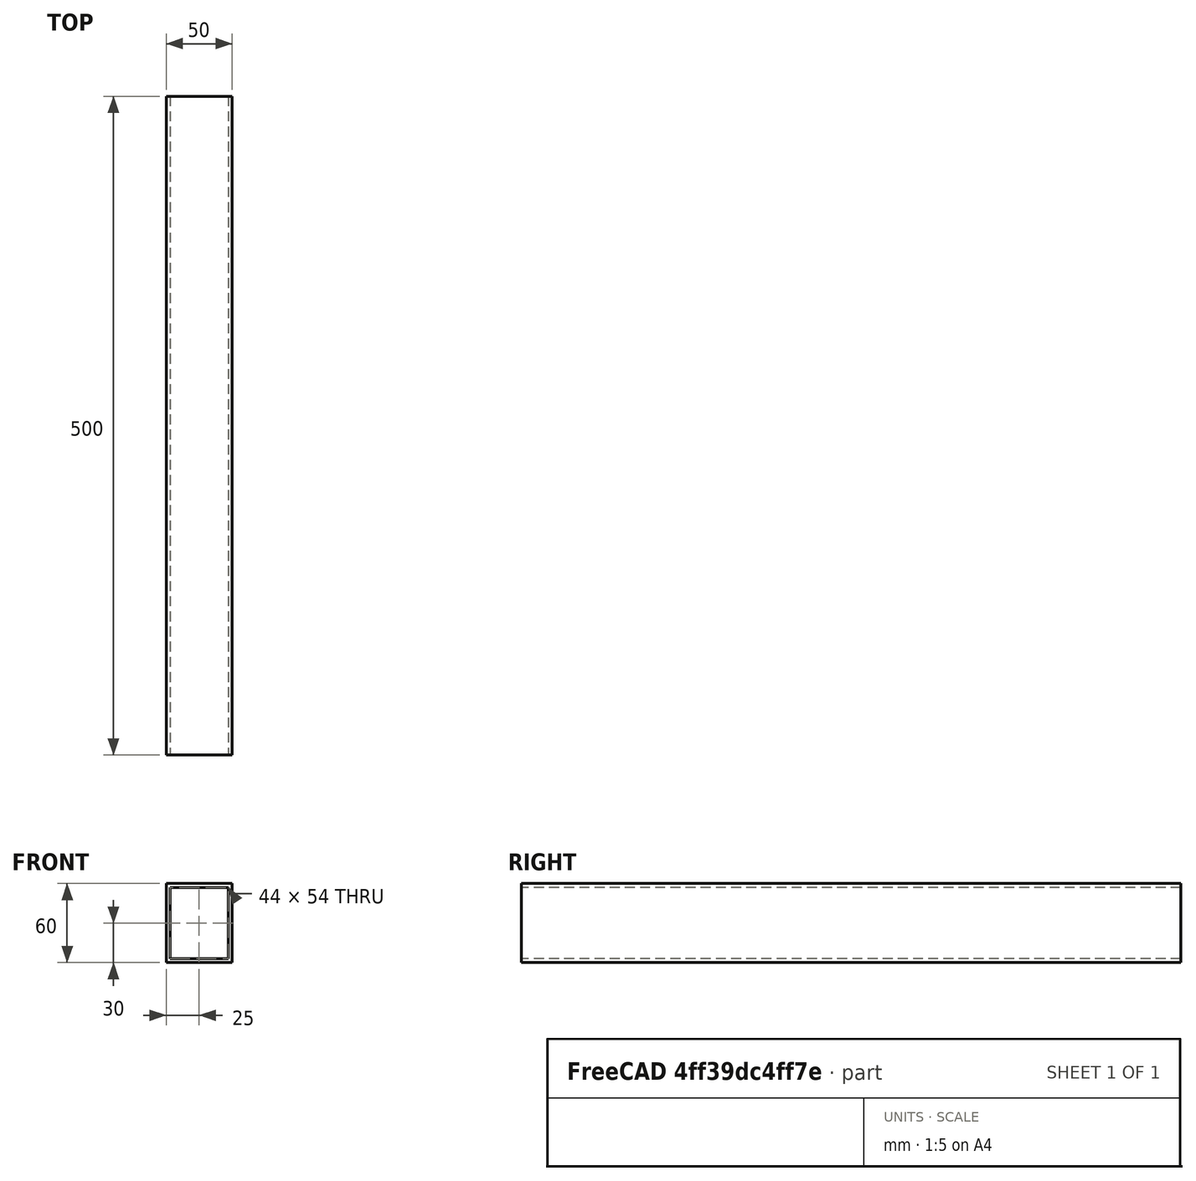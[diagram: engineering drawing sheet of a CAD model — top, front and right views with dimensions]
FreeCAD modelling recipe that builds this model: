
FCSTD DOCUMENT  (FreeCAD 0.20R29177 +426 (Git))
Label: beam_cross
License: All rights reserved
LicenseURL: http://en.wikipedia.org/wiki/All_rights_reserved
objects: Sketcher::SketchObject×1, PartDesign::Pad×1, PartDesign::Body×1
note: 4 computed .brp shape members not serialized (recipe doc carries the construction recipe); baked Part::Feature solids carry a one-line shape summary decoded from their .brp

FEATURE [Sketcher::SketchObject] Sketch
  FullyConstrained = true
  MapMode = 5
  Placement = pos=(0,0,0) rot=(1,0,0;1.5708rad)
  Support = -> [XZ_Plane]
  sketch-geometry (8):
    g0: LineSegment StartX=0 StartY=0 StartZ=0 EndX=50 EndY=0 EndZ=0
    g1: LineSegment StartX=50 StartY=0 StartZ=0 EndX=50 EndY=60 EndZ=0
    g2: LineSegment StartX=50 StartY=60 StartZ=0 EndX=0 EndY=60 EndZ=0
    g3: LineSegment StartX=0 StartY=60 StartZ=0 EndX=0 EndY=0 EndZ=0
    g4: LineSegment StartX=3 StartY=57 StartZ=0 EndX=47 EndY=57 EndZ=0
    g5: LineSegment StartX=47 StartY=57 StartZ=0 EndX=47 EndY=3 EndZ=0
    g6: LineSegment StartX=47 StartY=3 StartZ=0 EndX=3 EndY=3 EndZ=0
    g7: LineSegment StartX=3 StartY=3 StartZ=0 EndX=3 EndY=57 EndZ=0
  constraints (23):
    c: Coincident(g0,g1)
    c: Coincident(g1,g2)
    c: Coincident(g2,g3)
    c: Coincident(g3,g0)
    c: Horizontal(g0)
    c: Horizontal(g2)
    c: Vertical(g1)
    c: Vertical(g3)
    c: Coincident(g0,g-1)
    c: DistanceX(g2,g2) = 50
    c: DistanceY(g1,g1) = 60
    c: Coincident(g4,g5)
    c: Coincident(g5,g6)
    c: Coincident(g6,g7)
    c: Coincident(g7,g4)
    c: Horizontal(g4)
    c: Horizontal(g6)
    c: Vertical(g5)
    c: Vertical(g7)
    c: DistanceY(g4,g1) = 3
    c: DistanceX(g4,g1) = 3
    c: DistanceX(g0,g6) = 3
    c: DistanceY(g0,g6) = 3
FEATURE [PartDesign::Pad] Pad
  Direction = (0,-1,-2e-16)
  Length = 500
  Length2 = 10
  Placement = pos=(0,0,0) rot=(1,0,0;1.5708rad)
  Profile = -> Sketch
  ReferenceAxis = -> Sketch [N_Axis]
  Refine = true
  Type = 0
FEATURE [PartDesign::Body] Body
  Group = -> [Sketch,Pad]
  Origin = -> Origin
  Tip = -> Pad
